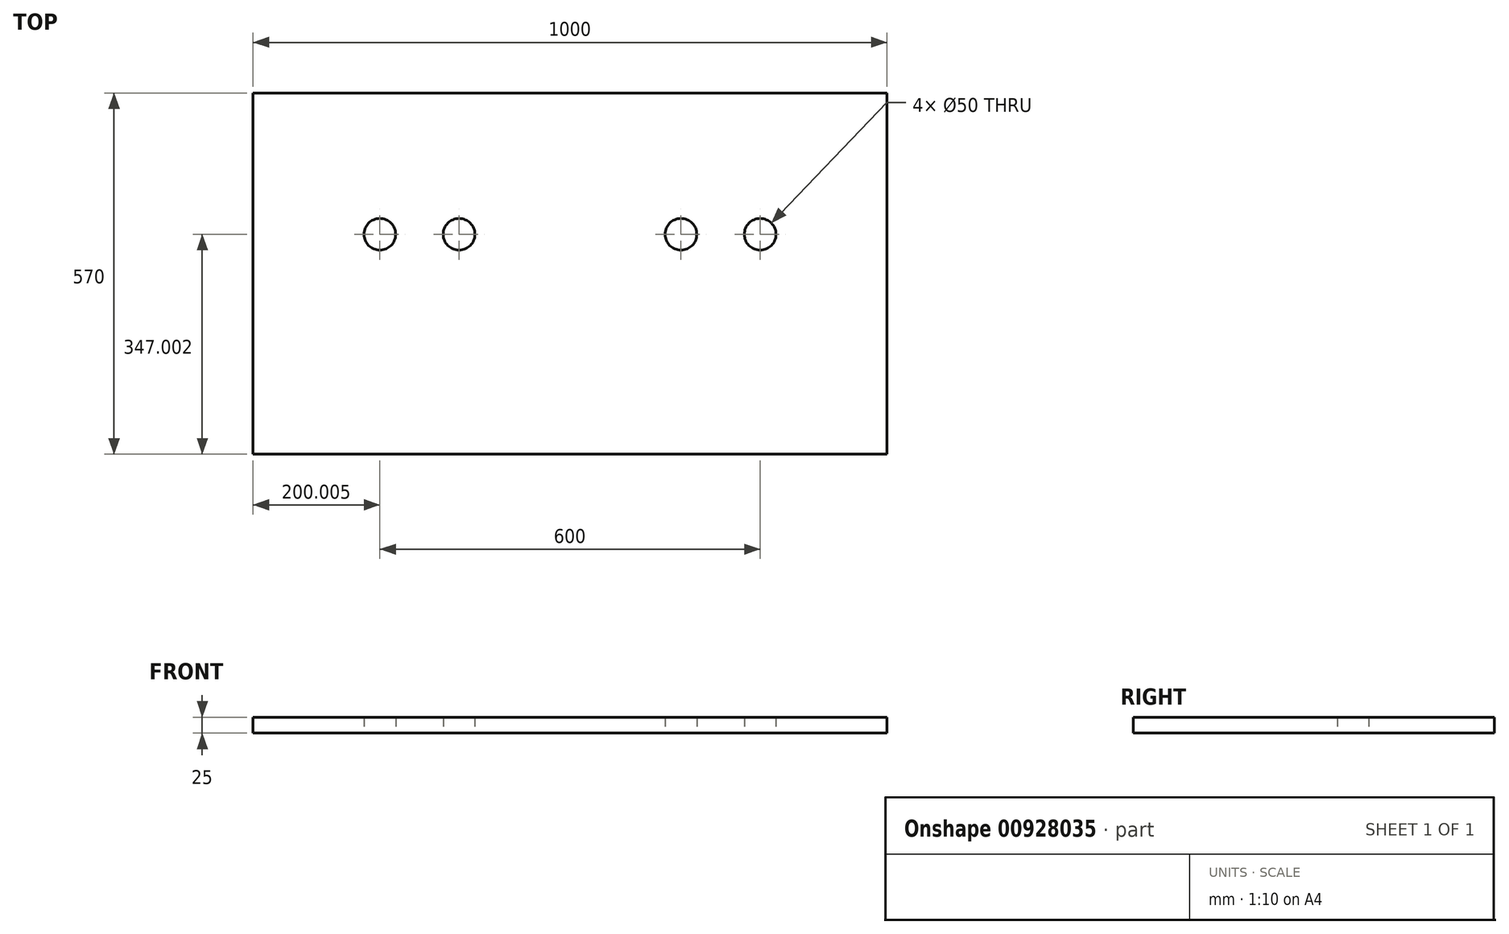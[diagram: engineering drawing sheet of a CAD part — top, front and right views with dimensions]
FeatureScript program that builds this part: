
annotation { "Feature Type Name" : "Feature", "Feature Type Description" : "" }
export const myFeature = defineFeature(function(context is Context, id is Id, definition is map)
    precondition{}
    {
        {
            var Q0;
            Q0=qCreatedBy(makeId("Top.planeOp"),FACE);
            var sketch = newSketch(context, id + "F0", { "sketchPlane" : qUnion([Q0])});
            skLineSegment(sketch, "E0.bottom", {"start": v(-829.64, 139.42) * mm, "end": v(170.36, 139.42) * mm});
            skLineSegment(sketch, "E0.top", {"start": v(-829.64, -430.58) * mm, "end": v(170.36, -430.58) * mm});
            skLineSegment(sketch, "E0.left", {"start": v(-829.64, 139.42) * mm, "end": v(-829.64, -430.58) * mm});
            skLineSegment(sketch, "E0.right", {"start": v(170.36, 139.42) * mm, "end": v(170.36, -430.58) * mm});
            skCircle(sketch, "E1", {"center": v(-629.64, -83.58) * mm, "radius": 25 * mm});
            skCircle(sketch, "E2", {"center": v(-504.64, -83.58) * mm, "radius": 25 * mm});
            skCircle(sketch, "E3", {"center": v(-154.64, -83.58) * mm, "radius": 25 * mm});
            skCircle(sketch, "E4", {"center": v(-29.64, -83.58) * mm, "radius": 25 * mm});
            skSolve(sketch);
        }
        {
            var Q0;
            Q0 = qSketchRegion(id + "F0", true);
            extrude(context, id + "F1", {"entities" : qUnion([Q0]), "depth" : 25 * mm, "offsetDistance" : 25 * mm});
        }
        {
            var Q0;
            Q0 = qSketchRegion(id + "F0", true);
            extrude(context, id + "F2", {"entities" : qUnion([Q0]), "operationType" : NewBodyOperationType.ADD, "depth" : 25 * mm, "offsetDistance" : 25 * mm});
        }
        {
            var Q0;
            Q0 = qSketchRegion(id + "F0", true);
            extrude(context, id + "F3", {"entities" : qUnion([Q0]), "operationType" : NewBodyOperationType.ADD, "depth" : 25 * mm, "offsetDistance" : 25 * mm});
        }
    });
